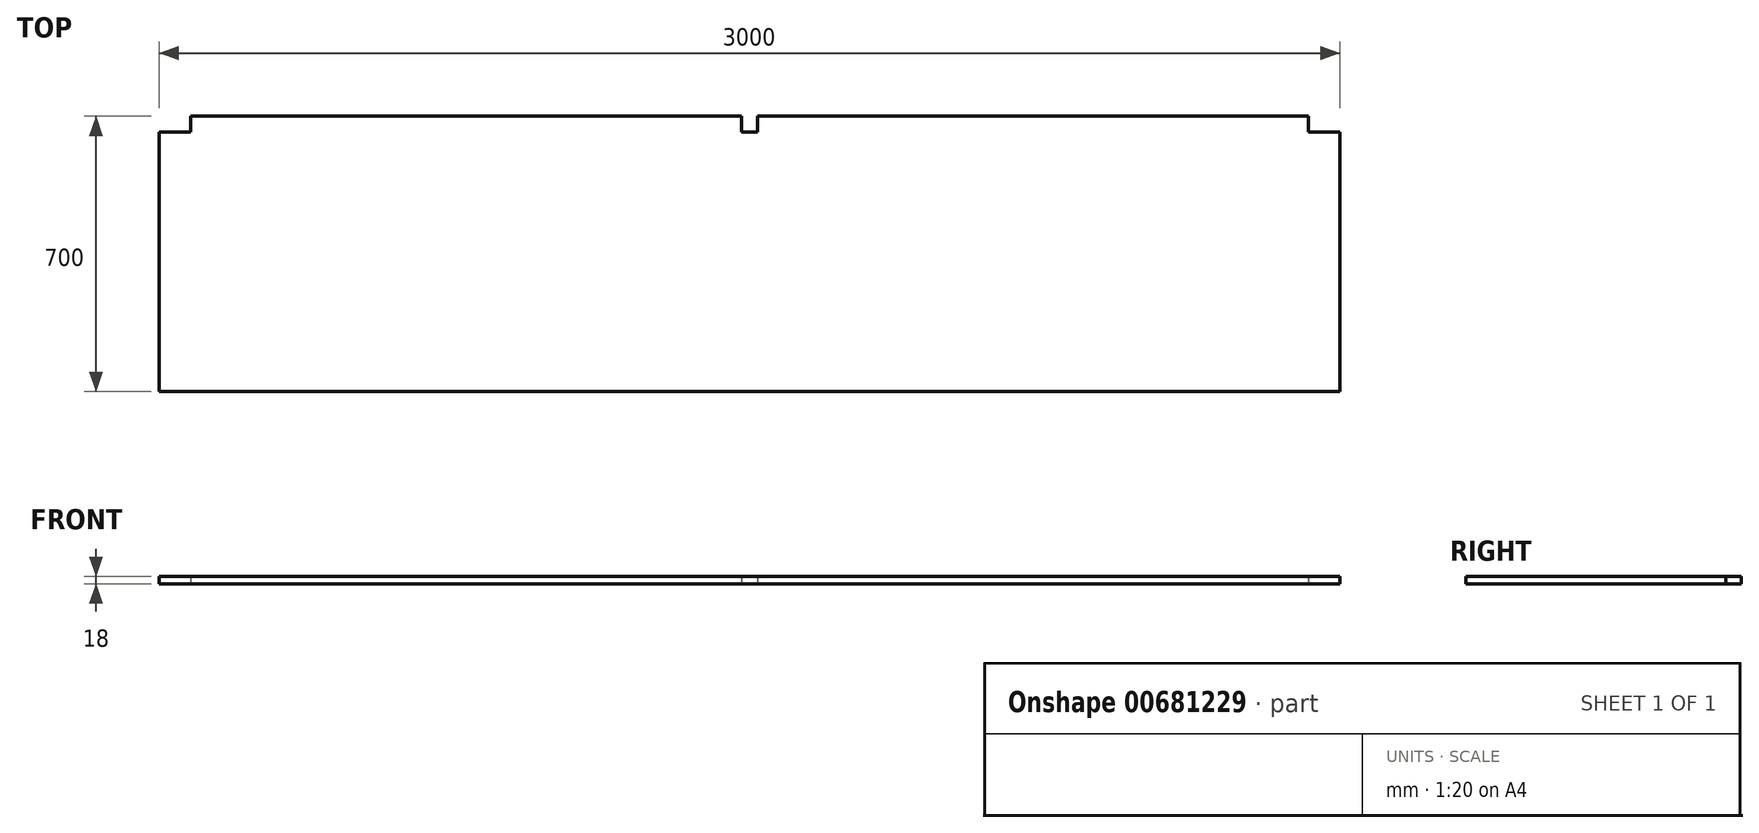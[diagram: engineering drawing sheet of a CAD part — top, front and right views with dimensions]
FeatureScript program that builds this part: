
annotation { "Feature Type Name" : "Feature", "Feature Type Description" : "" }
export const myFeature = defineFeature(function(context is Context, id is Id, definition is map)
    precondition{}
    {
        {
            var Q0;
            Q0=qCreatedBy(makeId("Top.planeOp"),FACE);
            var sketch = newSketch(context, id + "F0", { "sketchPlane" : qUnion([Q0])});
            skLineSegment(sketch, "E0.bottom", {"start": v(750, -350) * mm, "end": v(-750, -350) * mm});
            skLineSegment(sketch, "E0.top", {"start": v(730, 350) * mm, "end": v(-670, 350) * mm});
            skLineSegment(sketch, "E0.left", {"start": v(750, -350) * mm, "end": v(750, 310) * mm});
            skLineSegment(sketch, "E0.right", {"start": v(-750, -350) * mm, "end": v(-750, 310) * mm});
            skPoint(sketch, "E0.middle", {"position": v(0, 0) * mm});
            skLineSegment(sketch, "E1.top", {"start": v(-750, 310) * mm, "end": v(-670, 310) * mm});
            skLineSegment(sketch, "E1.right", {"start": v(-670, 350) * mm, "end": v(-670, 310) * mm});
            skPoint(sketch, "E2.orphan", {"position": v(-750, 350) * mm});
            skLineSegment(sketch, "E3.top", {"start": v(750, 310) * mm, "end": v(730, 310) * mm});
            skLineSegment(sketch, "E3.right", {"start": v(730, 350) * mm, "end": v(730, 310) * mm});
            skPoint(sketch, "E4.orphan", {"position": v(750, 350) * mm});
            skLineSegment(sketch, "E5.MirrorCS", {"start": v(2250, 310) * mm, "end": v(2170, 310) * mm});
            skLineSegment(sketch, "E6.MirrorCS", {"start": v(770, 350) * mm, "end": v(770, 310) * mm});
            skLineSegment(sketch, "E7.MirrorCS", {"start": v(750, 310) * mm, "end": v(770, 310) * mm});
            skLineSegment(sketch, "E8.MirrorCS", {"start": v(2170, 350) * mm, "end": v(2170, 310) * mm});
            skLineSegment(sketch, "E9.MirrorCS", {"start": v(2250, -350) * mm, "end": v(2250, 310) * mm});
            skLineSegment(sketch, "E10.MirrorCS", {"start": v(770, 350) * mm, "end": v(2170, 350) * mm});
            skLineSegment(sketch, "E11.MirrorCS", {"start": v(750, -350) * mm, "end": v(2250, -350) * mm});
            skPoint(sketch, "E12.MirrorP", {"position": v(1500, 0) * mm});
            skPoint(sketch, "E13.MirrorP", {"position": v(2250, 350) * mm});
            skSolve(sketch);
        }
        {
            var Q0;
            Q0=makeQuery(id+"F0.imprint","IMPRINT",FACE,{"disambiguationData":[TD([[makeQuery(id+"F0.imprint","IMPRINT",EDGE,{"derivedFrom":sQuery(id+"F0.wireOp",EDGE,"E0.bottom")}),-1.0]])]});
            var Q1;
            Q1=makeQuery(id+"F0.imprint","IMPRINT",FACE,{"disambiguationData":[TD([[makeQuery(id+"F0.imprint","IMPRINT",EDGE,{"derivedFrom":sQuery(id+"F0.wireOp",EDGE,"E0.left")}),-1.0]])]});
            extrude(context, id + "F1", {"entities" : qUnion([Q0, Q1]), "depth" : 18 * mm, "offsetDistance" : 25 * mm});
        }
    });
